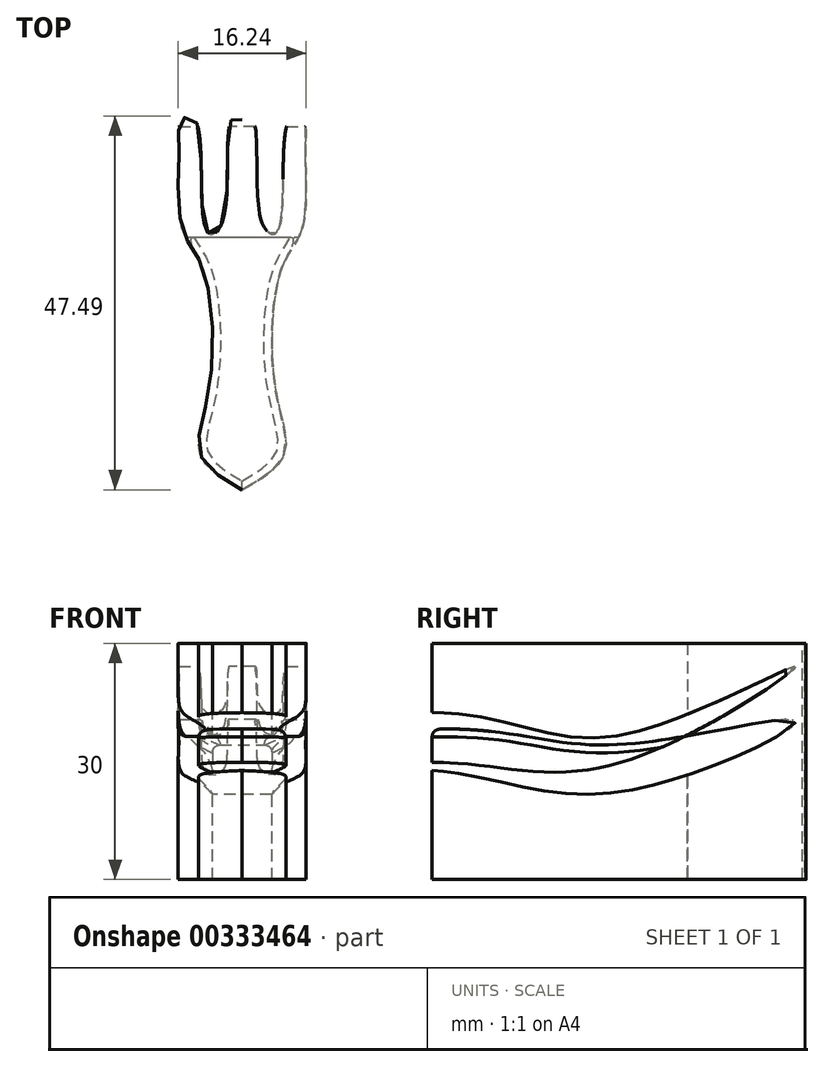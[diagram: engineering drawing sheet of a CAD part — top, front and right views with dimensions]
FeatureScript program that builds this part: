
annotation { "Feature Type Name" : "Feature", "Feature Type Description" : "" }
export const myFeature = defineFeature(function(context is Context, id is Id, definition is map)
    precondition{}
    {
        {
            var Q0;
            Q0=qCreatedBy(makeId("Top.planeOp"),FACE);
            var sketch = newSketch(context, id + "F0", { "sketchPlane" : qUnion([Q0])});
            skLineSegment(sketch, "E0.bottom", {"start": v(15, -50) * mm, "end": v(-15, -50) * mm});
            skLineSegment(sketch, "E0.top", {"start": v(15, 50) * mm, "end": v(-15, 50) * mm});
            skLineSegment(sketch, "E0.left", {"start": v(15, -50) * mm, "end": v(15, 50) * mm});
            skLineSegment(sketch, "E0.right", {"start": v(-15, -50) * mm, "end": v(-15, 50) * mm});
            skPoint(sketch, "E0.middle", {"position": v(0, 0) * mm});
            skSolve(sketch);
        }
        {
            var Q0;
            Q0=makeQuery(id+"F0.imprint","IMPRINT",FACE,{"disambiguationData":[TD([[makeQuery(id+"F0.imprint","IMPRINT",EDGE,{"derivedFrom":sQuery(id+"F0.wireOp",EDGE,"E0.bottom")}),-1.0]])]});
            extrude(context, id + "F1", {"entities" : qUnion([Q0]), "depth" : 30 * mm});
        }
        {
            var Q0;
            Q0=makeQuery(id+"F1.opExtrude","CAP_FACE",FACE,{"disambiguationData":[OSD([sQuery(id+"F0.wireOp",EDGE,"E0.bottom"),sQuery(id+"F0.wireOp",EDGE,"E0.top"),sQuery(id+"F0.wireOp",EDGE,"E0.left"),sQuery(id+"F0.wireOp",EDGE,"E0.right")])],"isStart":false});
            var sketch = newSketch(context, id + "F2", { "sketchPlane" : qUnion([Q0])});
            skPoint(sketch, "E1.0.internal.snap0", {"position": v(0, 50) * mm});
            skPoint(sketch, "E1.0.internal.orphan", {"position": v(0, 47.04) * mm});
            skFitSpline(sketch, "E2", {"points": [v(0, 47.04) * mm, v(1.37, 47.04) * mm, v(2.56, 33.85) * mm, v(4.47, 32.82) * mm, v(5.98, 47.04) * mm, v(7.65, 47.04) * mm, v(8.05, 43.39) * mm, v(7.65, 33.21) * mm, v(5.1, 28.44) * mm, v(4.21, 12.83) * mm, v(5.32, 4.45) * mm, v(0, 0) * mm], "startDerivative": vector(38.2, 17.36) * mm, "endDerivative": vector(-74.78, -42.25) * mm});
            skLineSegment(sketch, "E3", {"start": v(0, 47.04) * mm, "end": v(0, 0) * mm});
            skFitSpline(sketch, "E4.MirrorCS", {"points": [v(0, 47.04) * mm, v(-1.37, 47.04) * mm, v(-2.56, 33.85) * mm, v(-4.47, 32.82) * mm, v(-5.98, 47.04) * mm, v(-7.65, 47.04) * mm, v(-8.05, 43.39) * mm, v(-7.65, 33.21) * mm, v(-5.1, 28.44) * mm, v(-4.21, 12.83) * mm, v(-5.32, 4.45) * mm, v(0, 0) * mm], "startDerivative": vector(-38.2, 17.36) * mm, "endDerivative": vector(74.78, -42.25) * mm});
            skSolve(sketch);
        }
        {
            var Q0;
            Q0=makeQuery(id+"F1.opExtrude","SWEPT_FACE",FACE,{"disambiguationData":[OSD([sQuery(id+"F0.wireOp",EDGE,"E0.left")])]});
            var sketch = newSketch(context, id + "F3", { "sketchPlane" : qUnion([Q0])});
            skLineSegment(sketch, "E5.bottom", {"start": v(0, 30) * mm, "end": v(0, 30) * mm});
            skLineSegment(sketch, "E5.top", {"start": v(0, -30) * mm, "end": v(0, -30) * mm});
            skLineSegment(sketch, "E5.left", {"start": v(0, 30) * mm, "end": v(0, -30) * mm, "construction": true});
            skLineSegment(sketch, "E5.right", {"start": v(0, 30) * mm, "end": v(0, -30) * mm, "construction": true});
            skPoint(sketch, "E5.middle", {"position": v(0, 0) * mm});
            skLineSegment(sketch, "E6.bottom", {"start": v(46.14, 27.05) * mm, "end": v(-46.14, 27.05) * mm, "construction": true});
            skLineSegment(sketch, "E6.top", {"start": v(46.14, 2.74) * mm, "end": v(-46.14, 2.74) * mm, "construction": true});
            skLineSegment(sketch, "E6.left", {"start": v(46.14, 27.05) * mm, "end": v(46.14, 2.74) * mm, "construction": true});
            skLineSegment(sketch, "E6.right", {"start": v(-46.14, 27.05) * mm, "end": v(-46.14, 2.74) * mm, "construction": true});
            skPoint(sketch, "E6.middle", {"position": v(0, 14.9) * mm});
            skFitSpline(sketch, "E7", {"points": [v(46.14, 27.05) * mm, v(23.93, 18.34) * mm, v(0, 21.2) * mm, v(-41.5, 11.3) * mm, v(-32.94, 10.1) * mm, v(0, 14.9) * mm, v(24.08, 14.9) * mm, v(46.14, 27.05) * mm]});
            skPoint(sketch, "E8.1.internal.orphan", {"position": v(23.93, 17.15) * mm});
            skFitSpline(sketch, "E9", {"points": [v(46.14, 20.12) * mm, v(23.93, 17.15) * mm, v(0, 19.1) * mm, v(-40.48, 10.64) * mm, v(-31.25, 10.02) * mm, v(0, 13.85) * mm, v(23.93, 11.14) * mm, v(46.14, 20.12) * mm]});
            skSolve(sketch);
        }
        {
            var Q0;
            Q0=makeQuery(id+"F3.imprint","IMPRINT",FACE,{"disambiguationData":[TD([[makeQuery(id+"F3.imprint","IMPRINT",EDGE,{"derivedFrom":sQuery(id+"F3.wireOp",EDGE,"E7")}),-1.0]])]});
            var Q1;
            Q1=makeQuery(id+"F3.imprint","IMPRINT",FACE,{"disambiguationData":[TD([[makeQuery(id+"F3.imprint","IMPRINT",EDGE,{"derivedFrom":sQuery(id+"F3.wireOp",EDGE,"E9")}),-1.0]])]});
            extrude(context, id + "F4", {"entities" : qUnion([Q0, Q1]), "operationType" : NewBodyOperationType.REMOVE, "oppositeDirection" : true, "depth" : 30 * mm});
        }
        {
            var Q0;
            Q0=makeQuery(id+"F2.imprint","IMPRINT",FACE,{"disambiguationData":[TD([[makeQuery(id+"F2.imprint","IMPRINT",EDGE,{"derivedFrom":sQuery(id+"F2.wireOp",EDGE,"E2")}),1.0]])]});
            extrude(context, id + "F5", {"entities" : qUnion([Q0]), "operationType" : NewBodyOperationType.REMOVE, "oppositeDirection" : true, "depth" : 30 * mm});
        }
        {
            var Q0;
            Q0=makeQuery(id+"F5.boolean.opBoolean","INTERSECT",EDGE,{"disambiguationData":[OD(1.0)],"derivedFrom":[makeQuery(id+"F4.boolean.opBoolean","COPY",FACE,{"derivedFrom":makeQuery(id+"F4.opExtrude","SWEPT_FACE",FACE,{"disambiguationData":[OSD([sQuery(id+"F3.wireOp",EDGE,"E9")])]})}),makeQuery(id+"F5.opExtrude","SWEPT_FACE",FACE,{"disambiguationData":[OSD([sQuery(id+"F2.wireOp",EDGE,"E4.MirrorCS")])]})]});
            var Q1;
            Q1=makeQuery(id+"F5.boolean.opBoolean","INTERSECT",EDGE,{"disambiguationData":[OD(1.0)],"derivedFrom":[makeQuery(id+"F4.boolean.opBoolean","COPY",FACE,{"derivedFrom":makeQuery(id+"F4.opExtrude","SWEPT_FACE",FACE,{"disambiguationData":[OSD([sQuery(id+"F3.wireOp",EDGE,"E9")])]})}),makeQuery(id+"F5.opExtrude","SWEPT_FACE",FACE,{"disambiguationData":[OSD([sQuery(id+"F2.wireOp",EDGE,"E2")])]})]});
            fillet(context, id + "F6", {"entities" : qUnion([Q0, Q1]), "radius" : 1 * mm, "tangentPropagation" : true, "allowEdgeOverflow" : false});
        }
    });
